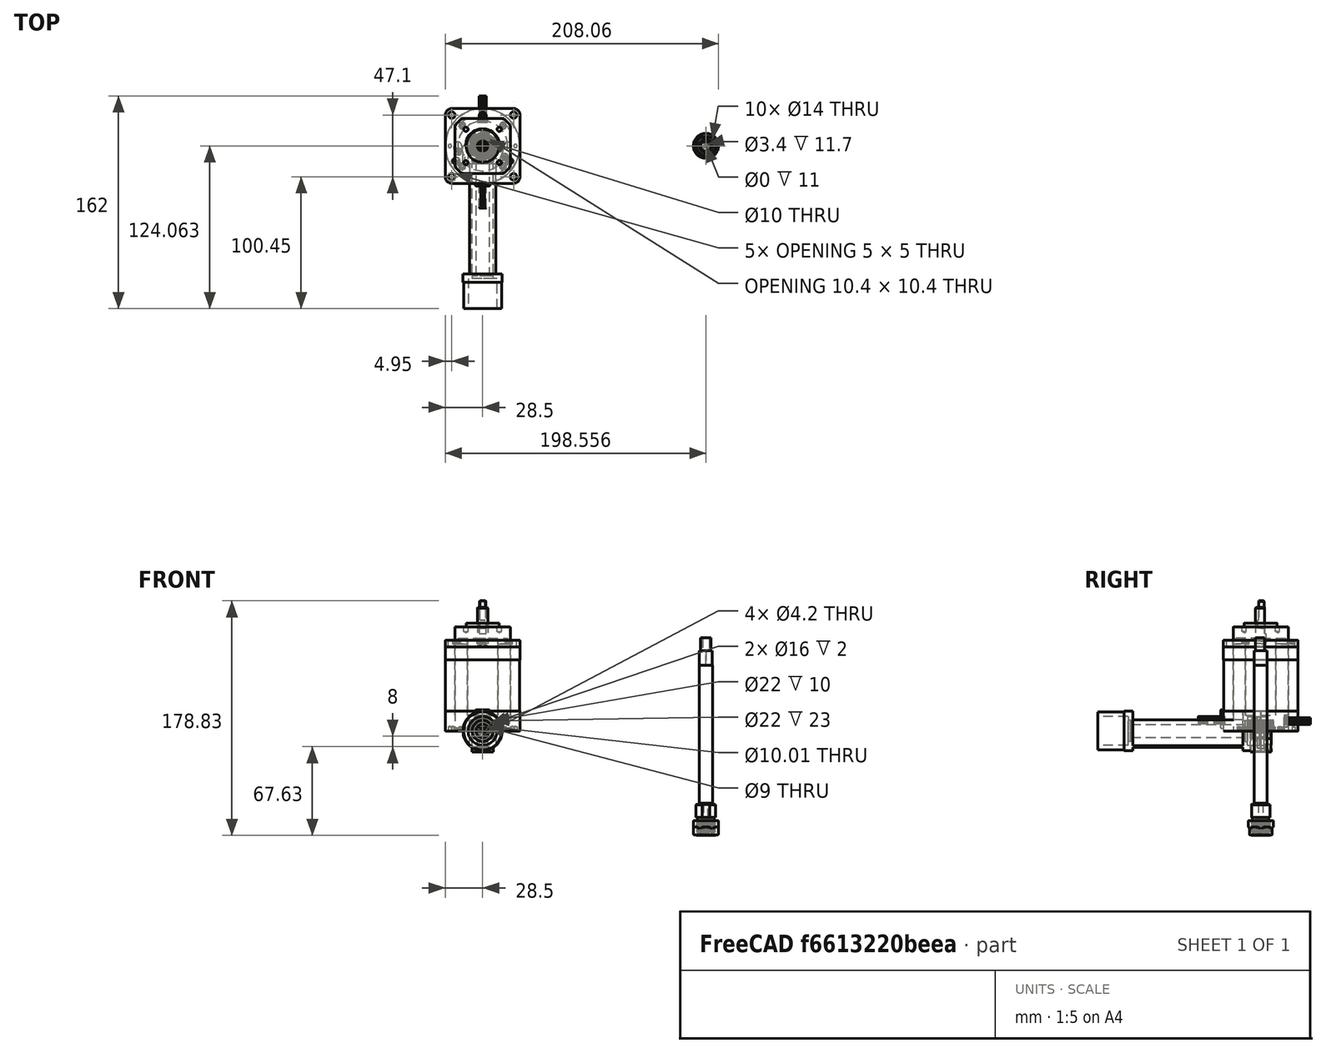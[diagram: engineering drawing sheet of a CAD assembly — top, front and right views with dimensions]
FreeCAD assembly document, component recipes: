
FREECAD ASSEMBLY — COMPONENT RECIPES ("ToolPostDrill")

This assembly document has 13 components, labeled P0..P12 below (a component is one placed body or linked part). 8 of them carry a construction recipe — the FreeCAD feature program that regenerates the part from scratch, quoted from this document or its linked companion documents; the rest are supplied as boundary geometry only. No exploded tour is included for this assembly.
COMPONENT P0 — geometry summary ("Bearing"; no construction recipe available for this part):
  bounding box: 22.0 x 22.0 x 6.0 mm
  tessellated surface: 480 triangles
  volume: 1254 mm^3 (43% of its bounding box)
  symmetry: 2-fold rotationally symmetric about the x axis; 4-fold rotationally symmetric about the y axis; 2-fold rotationally symmetric about the z axis; mirror-symmetric across its y mid-plane, z mid-plane
COMPONENT P1 — recipe-attached ("BLDC adapter", modeled in this document).
Construction recipe (the document's own serialized feature program — sketch geometry with constraints, then the solid features built on it; lengths are millimeters unless a unit is written):

FEATURE [Sketcher::SketchObject] Sketch017
  FullyConstrained = true
  MapMode = 5
  Support = -> [XY_Plane019]
  expr: Constraints[2] = Spreadsheet.ShaftDiameter
  expr: Constraints[3] = Spreadsheet.SpacerOuterDiameter
  sketch-geometry (2):
    g0: Circle CenterX=0 CenterY=0 CenterZ=0 NormalX=0 NormalY=0 NormalZ=1 AngleXU=0 Radius=5
    g1: Circle CenterX=0 CenterY=0 CenterZ=0 NormalX=0 NormalY=0 NormalZ=1 AngleXU=0 Radius=10.95
  constraints (4):
    c: Coincident(g0,g-1)
    c: Coincident(g1,g0)
    c: Diameter(g0) = 10
    c: Diameter(g1) = 21.9
FEATURE [PartDesign::Pad] Pad007
  Direction = (0,0,1)
  Length = 4
  Length2 = 10
  Profile = -> Sketch017
  ReferenceAxis = -> Sketch017 [N_Axis]
  Type = 0
  expr: Length = Spreadsheet.FrontSpacerWidth
FEATURE [PartDesign::Chamfer] Chamfer
  Angle = 45
  Base = -> Pad007 [Face4,Face3]
  BaseFeature = -> Pad007
  ChamferType = 0
  FlipDirection = false
  Size = 0.25
  Size2 = 1
  SupportTransform = false
  UseAllEdges = false
FEATURE [Sketcher::SketchObject] Sketch023
  FullyConstrained = true
  MapMode = 5
  Placement = pos=(0,0,4) rot=(0,0,1;0rad)
  Support = -> [Pad007]
  expr: Constraints[2] = Spreadsheet.BearingInnerPocketDiameter
  expr: Constraints[3] = Spreadsheet.SpacerOuterDiameter
  sketch-geometry (2):
    g0: Circle CenterX=0 CenterY=0 CenterZ=0 NormalX=0 NormalY=0 NormalZ=1 AngleXU=0 Radius=8
    g1: Circle CenterX=0 CenterY=0 CenterZ=0 NormalX=0 NormalY=0 NormalZ=1 AngleXU=0 Radius=10.95
  constraints (4):
    c: Coincident(g0,g-1)
    c: Coincident(g1,g0)
    c: Diameter(g0) = 16
    c: Diameter(g1) = 21.9
FEATURE [PartDesign::Pocket] Pocket009
  BaseFeature = -> Chamfer
  Direction = (0,0,-1)
  Length = 1
  Length2 = 5
  Profile = -> Sketch023
  ReferenceAxis = -> Sketch023 [N_Axis]
  Type = 0
FEATURE [PartDesign::Body] Body005  label="Body006"
  Group = -> [Sketch017,Pad007,Chamfer,Sketch023,Pocket009]
  Origin = -> Origin019
  Tip = -> Pocket009
COMPONENT P2 — geometry summary ("TopSlide"; no construction recipe available for this part):
  bounding box: 180.0 x 86.8 x 80.0 mm
  tessellated surface: 68 triangles
  volume: 648582 mm^3 (52% of its bounding box)
COMPONENT P3 — geometry summary ("ConnectorHousing"; no construction recipe available for this part):
  bounding box: 49.0 x 36.9 x 28.0 mm
  tessellated surface: 568 triangles
  volume: 17478 mm^3 (35% of its bounding box)
  symmetry: mirror-symmetric across its y mid-plane
COMPONENT P4 — recipe-attached ("LockNut", modeled in this document).
Construction recipe (the document's own serialized feature program — sketch geometry with constraints, then the solid features built on it; lengths are millimeters unless a unit is written):

FEATURE [Sketcher::SketchObject] Sketch024
  FullyConstrained = true
  MapMode = 5
  Placement = pos=(0,0,0) rot=(0.57735,0.57735,0.57735;2.0944rad)
  Support = -> [YZ_Plane025]
  expr: Constraints[13] = Spreadsheet.LockNutThreadDiameter / 2
  expr: Constraints[14] = Spreadsheet.LockNutDiameter / 2
  expr: Constraints[15] = Spreadsheet.BearingDiameterBase / 2
  expr: Constraints[17] = Spreadsheet.LockNutThickness
  sketch-geometry (6):
    g0: LineSegment StartX=0 StartY=10.9 StartZ=0 EndX=4.5 EndY=10.9 EndZ=0
    g1: LineSegment StartX=4.5 StartY=10.9 StartZ=0 EndX=4.5 EndY=7 EndZ=0
    g2: LineSegment StartX=4.5 StartY=7 StartZ=0 EndX=5 EndY=7 EndZ=0
    g3: LineSegment StartX=5 StartY=7 StartZ=0 EndX=5 EndY=4.5 EndZ=0
    g4: LineSegment StartX=5 StartY=4.5 StartZ=0 EndX=0 EndY=4.5 EndZ=0
    g5: LineSegment StartX=0 StartY=4.5 StartZ=0 EndX=0 EndY=10.9 EndZ=0
  constraints (18):
    c: PointOnObject(g0,g-2)
    c: Horizontal(g0)
    c: Coincident(g0,g1)
    c: Vertical(g1)
    c: Coincident(g1,g2)
    c: Horizontal(g2)
    c: Coincident(g2,g3)
    c: Vertical(g3)
    c: Coincident(g3,g4)
    c: PointOnObject(g4,g-2)
    c: Horizontal(g4)
    c: Coincident(g4,g5)
    c: Coincident(g5,g0)
    c: DistanceY(g-1,g4) = 4.5
    c: DistanceY(g-1,g0) = 10.9
    c: DistanceY(g-1,g2) = 7
    c: DistanceX(g2,g2) = 0.5
    c: DistanceX(g4,g4) = 5
FEATURE [PartDesign::Revolution] Revolution
  Angle = 360
  Axis = (1e-16,1,-1e-16)
  Base = (0,0,0)
  Placement = pos=(0,0,0) rot=(0.57735,0.57735,0.57735;2.0944rad)
  Profile = -> Sketch024
  ReferenceAxis = -> Y_Axis025
FEATURE [Sketcher::SketchObject] Sketch025
  FullyConstrained = true
  MapMode = 5
  Placement = pos=(0,-5e-16,0) rot=(0.57735,0.57735,-0.57735;2.0944rad)
  Support = -> [Revolution]
  expr: Constraints[2] = Spreadsheet.LockNutBoltSeparation
  expr: Constraints[3] = Spreadsheet.LockNutBoltDiameter
  sketch-geometry (2):
    g0: Circle CenterX=0 CenterY=8 CenterZ=0 NormalX=0 NormalY=0 NormalZ=1 AngleXU=0 Radius=1.5
    g1: Circle CenterX=0 CenterY=-8 CenterZ=0 NormalX=0 NormalY=0 NormalZ=1 AngleXU=0 Radius=1.5
  constraints (5):
    c: PointOnObject(g0,g-2)
    c: Symmetric(g0,g1,g-1)
    c: DistanceY(g1,g0) = 16
    c: Diameter(g0) = 3
    c: Equal(g0,g1)
FEATURE [PartDesign::Pocket] Pocket010
  BaseFeature = -> Revolution
  Direction = (2e-16,1,-4e-16)
  Length = 5
  Length2 = 5
  Placement = pos=(0,0,0) rot=(0.57735,0.57735,0.57735;2.0944rad)
  Profile = -> Sketch025
  ReferenceAxis = -> Sketch025 [N_Axis]
  Type = 1
FEATURE [PartDesign::Body] Body007  label="LockNutNut"
  Group = -> [Sketch024,Revolution,Sketch025,Pocket010]
  Origin = -> Origin025
  Tip = -> Pocket010
FEATURE [Sketcher::SketchObject] Sketch026
  FullyConstrained = true
  MapMode = 5
  Placement = pos=(0,0,0) rot=(1,0,0;1.5708rad)
  Support = -> [XZ_Plane026]
  expr: Constraints[2] = Spreadsheet.LockNutThreadDiameter
  expr: Constraints[3] = Spreadsheet.LockNutBoltThreadDiameter
  expr: Constraints[5] = Spreadsheet.LockNutDiameter
  expr: Constraints[7] = Spreadsheet.LockNutBoltSeparation
  sketch-geometry (4):
    g0: Circle CenterX=0 CenterY=0 CenterZ=0 NormalX=0 NormalY=0 NormalZ=1 AngleXU=0 Radius=4.5
    g1: Circle CenterX=0 CenterY=0 CenterZ=0 NormalX=0 NormalY=0 NormalZ=1 AngleXU=0 Radius=10.9
    g2: Circle CenterX=-8 CenterY=0 CenterZ=0 NormalX=0 NormalY=0 NormalZ=1 AngleXU=0 Radius=1.25
    g3: Circle CenterX=8 CenterY=0 CenterZ=0 NormalX=0 NormalY=0 NormalZ=1 AngleXU=0 Radius=1.25
  constraints (9):
    c: Coincident(g0,g-1)
    c: Coincident(g1,g0)
    c: Diameter(g0) = 9
    c: Diameter(g2) = 2.5
    c: Equal(g2,g3)
    c: Diameter(g1) = 21.8
    c: Symmetric(g3,g2,g0)
    c: Distance(g2,g3) = 16
    c: PointOnObject(g2,g-1)
FEATURE [PartDesign::Pad] Pad009
  Direction = (0,-1,-2e-16)
  Length = 3
  Length2 = 10
  Placement = pos=(0,0,0) rot=(1,0,0;1.5708rad)
  Profile = -> Sketch026
  ReferenceAxis = -> Sketch026 [N_Axis]
  Type = 0
  expr: Length = Spreadsheet.LockNutWasherThickness
FEATURE [PartDesign::CoordinateSystem] Back
  AttacherType = Attacher::AttachEngine3D
  MapMode = 11
  Placement = pos=(0,-3,7e-16) rot=(0.57735,-0.57735,0.57735;2.0944rad)
  Support = -> [Pad009]
FEATURE [PartDesign::Body] Body008  label="LockNutDisk"
  Group = -> [Sketch026,Pad009,Back]
  Origin = -> Origin026
  Placement = pos=(0,-1,0) rot=(0,0,1;0rad)
  Tip = -> Pad009
COMPONENT P5 — recipe-attached ("Housing", modeled in this document).
Construction recipe (the document's own serialized feature program — sketch geometry with constraints, then the solid features built on it; lengths are millimeters unless a unit is written):

FEATURE [Sketcher::SketchObject] Sketch
  FullyConstrained = true
  MapMode = 5
  Placement = pos=(0,0,0) rot=(1,0,0;1.5708rad)
  Support = -> [XZ_Plane005]
  expr: Constraints[1] = Spreadsheet.HousingDiameter
  sketch-geometry (1):
    g0: Circle CenterX=0 CenterY=0 CenterZ=0 NormalX=0 NormalY=0 NormalZ=1 AngleXU=0 Radius=14.95
  constraints (2):
    c: Coincident(g0,g-1)
    c: Diameter(g0) = 29.9
FEATURE [PartDesign::Pad] Pad001  label="Housing001"
  Direction = (0,-1,-2e-16)
  Length = 124
  Length2 = 10
  Placement = pos=(0,0,0) rot=(1,0,0;1.5708rad)
  Profile = -> Sketch
  ReferenceAxis = -> Sketch [N_Axis]
  Type = 0
  expr: Length = Spreadsheet.HousingLength
FEATURE [Sketcher::SketchObject] Sketch001
  FullyConstrained = true
  MapMode = 5
  Placement = pos=(0,0,0) rot=(-1,0,0;1.5708rad)
  Support = -> [Pad001]
  expr: Constraints[1] = Spreadsheet.BearingDiameter
  sketch-geometry (1):
    g0: Circle CenterX=0 CenterY=0 CenterZ=0 NormalX=0 NormalY=0 NormalZ=1 AngleXU=0 Radius=11
  constraints (2):
    c: Coincident(g0,g-1)
    c: Diameter(g0) = 22
FEATURE [PartDesign::Pocket] Pocket  label="FrontBearingPocket"
  BaseFeature = -> Pad001
  Direction = (0,-1,-2e-16)
  Length = 10
  Length2 = 5
  Placement = pos=(0,0,0) rot=(1,0,0;1.5708rad)
  Profile = -> Sketch001
  ReferenceAxis = -> Sketch001 [N_Axis]
  Type = 0
  expr: Length = Spreadsheet.FrontBearingPocketDepth
FEATURE [Sketcher::SketchObject] Sketch002
  FullyConstrained = true
  MapMode = 5
  Placement = pos=(0,-10,0) rot=(-1,0,0;1.5708rad)
  Support = -> [Pocket]
  expr: Constraints[1] = Spreadsheet.ShaftBoringDiameter
  sketch-geometry (1):
    g0: Circle CenterX=0 CenterY=0 CenterZ=0 NormalX=0 NormalY=0 NormalZ=1 AngleXU=0 Radius=5.005
  constraints (2):
    c: Coincident(g0,g-1)
    c: Diameter(g0) = 10.01
FEATURE [Sketcher::SketchObject] Sketch004
  AttachmentOffset = pos=(0,0,13.5) rot=(0,0,1;0rad)
  FullyConstrained = true
  MapMode = 5
  Placement = pos=(0,-13.5,-3e-15) rot=(1,0,0;1.5708rad)
  Support = -> [XZ_Plane005]
  expr: .AttachmentOffset.Base.z = Spreadsheet.ToolPostPocketPositionH
  expr: Constraints[13] = Spreadsheet.HousingDiameter + 1
  expr: Constraints[2] = Spreadsheet.ToolHeight
  expr: Constraints[3] = Spreadsheet.HousingDiameter + 1
  expr: Constraints[5] = Spreadsheet.ToolHolderHeigth
  expr: Constraints[7] = Spreadsheet.ShaftPosition
  sketch-geometry (13):
    g0: LineSegment StartX=-9.29289 StartY=-12.5 StartZ=0 EndX=9.29289 EndY=-12.5 EndZ=0
    g1: LineSegment StartX=15.45 StartY=-15.45 StartZ=0 EndX=-15.45 EndY=-15.45 EndZ=0
    g2: LineSegment StartX=-10 StartY=8.5 StartZ=0 EndX=10 EndY=8.5 EndZ=0
    g3: LineSegment StartX=-10 StartY=-11.7929 StartZ=0 EndX=-10 EndY=8.5 EndZ=0
    g4: LineSegment StartX=10 StartY=8.5 StartZ=0 EndX=10 EndY=-11.7929 EndZ=0
    g5: LineSegment StartX=-15.45 StartY=-15.45 StartZ=0 EndX=-15.45 EndY=15.45 EndZ=0
    g6: LineSegment StartX=-15.45 StartY=15.45 StartZ=0 EndX=15.45 EndY=15.45 EndZ=0
    g7: LineSegment StartX=15.45 StartY=15.45 StartZ=0 EndX=15.45 EndY=-15.45 EndZ=0
    g8: GeomPoint X=-15.45 Y=15.45 Z=0
    g9: GeomPoint X=-10 Y=8.5 Z=0
    g10: GeomPoint X=10 Y=8.5 Z=0
    g11: LineSegment StartX=-10 StartY=-11.7929 StartZ=0 EndX=-9.29289 EndY=-12.5 EndZ=0
    g12: LineSegment StartX=10 StartY=-11.7929 StartZ=0 EndX=9.29289 EndY=-12.5 EndZ=0
  constraints (33):
    c: Horizontal(g0)
    c: Symmetric(g1,g1,g-2)
    c: DistanceY(g0,g-1) = 12.5
    c: DistanceX(g1,g1) = 30.9
    c: Symmetric(g9,g10,g-2)
    c: DistanceY(g0,g10) = 21
    c: Vertical(g3)
    c: DistanceX(g-1,g10) = 10
    c: Coincident(g1,g5)
    c: Vertical(g5)
    c: Horizontal(g6)
    c: Coincident(g6,g7)
    c: Coincident(g7,g1)
    c: DistanceY(g7,g7) = 30.9
    c: PointOnObject(g8,g6)
    c: PointOnObject(g8,g5)
    c: Symmetric(g6,g1,g-1)
    c: PointOnObject(g9,g2)
    c: PointOnObject(g9,g3)
    c: PointOnObject(g10,g2)
    c: PointOnObject(g10,g4)
    c: Vertical(g4)
    c: Coincident(g3,g2)
    c: Coincident(g4,g2)
    c: Coincident(g5,g6)
    c: Coincident(g4,g12)
    c: Coincident(g12,g0)
    c: Angle(g12,g0) = 2.35619
    c: Coincident(g3,g11)
    c: Coincident(g11,g0)
    c: Angle(g0,g11) = 2.35619
    c: Distance(g11) = 1
    c: Equal(g11,g12)
FEATURE [Sketcher::SketchObject] Sketch021
  FullyConstrained = true
  MapMode = 5
  Placement = pos=(0,-10,0) rot=(-1,0,0;1.5708rad)
  Support = -> [Pocket]
  expr: Constraints[1] = Spreadsheet.BearingInnerPocketDiameter
  sketch-geometry (1):
    g0: Circle CenterX=0 CenterY=0 CenterZ=0 NormalX=0 NormalY=0 NormalZ=1 AngleXU=0 Radius=8
  constraints (2):
    c: Coincident(g0,g-1)
    c: Diameter(g0) = 16
FEATURE [PartDesign::Pocket] Pocket007  label="FrontBearingInnerPocket"
  BaseFeature = -> Pocket
  Direction = (0,-1,-2e-16)
  Length = 2
  Length2 = 5
  Placement = pos=(0,0,0) rot=(1,0,0;1.5708rad)
  Profile = -> Sketch021
  ReferenceAxis = -> Sketch021 [N_Axis]
  Type = 0
  expr: Length = Spreadsheet.BearingInnerPocketDepth
FEATURE [PartDesign::Pocket] Pocket001  label="ShaftPocket"
  BaseFeature = -> Pocket007
  Direction = (0,-1,-2e-16)
  Length = 5
  Length2 = 5
  Placement = pos=(0,0,0) rot=(1,0,0;1.5708rad)
  Profile = -> Sketch002
  ReferenceAxis = -> Sketch002 [N_Axis]
  Type = 1
FEATURE [Sketcher::SketchObject] Sketch003
  FullyConstrained = true
  MapMode = 5
  Placement = pos=(0,-124,3e-16) rot=(1,0,0;1.5708rad)
  Support = -> [Pocket001]
  expr: Constraints[1] = Spreadsheet.BearingDiameter
  sketch-geometry (1):
    g0: Circle CenterX=0 CenterY=0 CenterZ=0 NormalX=0 NormalY=0 NormalZ=1 AngleXU=0 Radius=11
  constraints (2):
    c: Coincident(g0,g-1)
    c: Diameter(g0) = 22
FEATURE [PartDesign::Pocket] Pocket002  label="BackBearingPocket"
  BaseFeature = -> Pocket001
  Direction = (0,1,2e-16)
  Length = 23
  Length2 = 5
  Placement = pos=(0,0,0) rot=(1,0,0;1.5708rad)
  Profile = -> Sketch003
  ReferenceAxis = -> Sketch003 [N_Axis]
  Type = 0
  expr: Length = Spreadsheet.BackBearingPocketDepth
FEATURE [Sketcher::SketchObject] Sketch022
  FullyConstrained = true
  MapMode = 5
  Placement = pos=(0,-101,2.24e-14) rot=(1,0,0;1.5708rad)
  Support = -> [Pocket002]
  expr: Constraints[1] = Spreadsheet.BearingInnerPocketDiameter
  sketch-geometry (1):
    g0: Circle CenterX=0 CenterY=0 CenterZ=0 NormalX=0 NormalY=0 NormalZ=1 AngleXU=0 Radius=8
  constraints (2):
    c: Coincident(g0,g-1)
    c: Diameter(g0) = 16
FEATURE [PartDesign::Pocket] Pocket008  label="BackBearingInnerPocket"
  BaseFeature = -> Pocket002
  Direction = (0,1,-2e-16)
  Length = 2
  Length2 = 5
  Placement = pos=(0,0,0) rot=(1,0,0;1.5708rad)
  Profile = -> Sketch022
  ReferenceAxis = -> Sketch022 [N_Axis]
  Type = 0
  expr: Length = Spreadsheet.BearingInnerPocketDepth
FEATURE [PartDesign::Pocket] Pocket003  label="ToolPostPocket"
  BaseFeature = -> Pocket008
  Direction = (0,1,2e-16)
  Length = 84
  Length2 = 5
  Placement = pos=(0,0,0) rot=(1,0,0;1.5708rad)
  Profile = -> Sketch004
  ReferenceAxis = -> Sketch004 [N_Axis]
  Reversed = true
  Type = 0
  expr: Length = Spreadsheet.ToolPostPocketLength
FEATURE [Sketcher::SketchObject] Sketch015
  FullyConstrained = true
  MapMode = 5
  Placement = pos=(0,-124,3e-16) rot=(1,0,0;1.5708rad)
  Support = -> [Pocket003]
  expr: Constraints[1] = Spreadsheet.MountingShaftDiameter
  expr: Constraints[3] = Spreadsheet.HousingDiameter + 1
  sketch-geometry (2):
    g0: Circle CenterX=0 CenterY=0 CenterZ=0 NormalX=0 NormalY=0 NormalZ=1 AngleXU=0 Radius=14.45
    g1: Circle CenterX=0 CenterY=0 CenterZ=0 NormalX=0 NormalY=0 NormalZ=1 AngleXU=0 Radius=15.45
  constraints (4):
    c: Coincident(g0,g-1)
    c: Diameter(g0) = 28.9
    c: Coincident(g1,g0)
    c: Diameter(g1) = 30.9
FEATURE [PartDesign::Pocket] Pocket005  label="MountingShaftPocket"
  BaseFeature = -> Pocket003
  Direction = (0,1,2e-16)
  Length = 20
  Length2 = 5
  Placement = pos=(0,0,0) rot=(1,0,0;1.5708rad)
  Profile = -> Sketch015
  ReferenceAxis = -> Sketch015 [N_Axis]
  Type = 0
  expr: Length = Spreadsheet.MountingShaftLength
FEATURE [PartDesign::Body] Body001  label="HousingBody"
  Group = -> [Sketch,Pad001,Sketch001,Pocket,Pocket007,Sketch002,Pocket001,Sketch003,Pocket002,Pocket008,Sketch004,Pocket003,Sketch015,Pocket005,Sketch021,Sketch022]
  Origin = -> Origin005
  Tip = -> Pocket005
COMPONENT P6 — geometry summary ("Spindle"; no construction recipe available for this part):
  bounding box: 150.6 x 19.0 x 18.8 mm
  tessellated surface: 3,004 triangles
  volume: 13659 mm^3 (25% of its bounding box)
COMPONENT P7 — geometry summary ("BLDCmotor"; no construction recipe available for this part):
  bounding box: 94.1 x 76.0 x 57.0 mm
  tessellated surface: 5,510 triangles
  volume: 180203 mm^3 (44% of its bounding box)
COMPONENT P8 — recipe-attached ("BevelGearSpindle", modeled in this document).
Construction recipe (the document's own serialized feature program — sketch geometry with constraints, then the solid features built on it; lengths are millimeters unless a unit is written):

FEATURE [Sketcher::SketchObject] Sketch031
  FullyConstrained = true
  MapMode = 5
  Support = -> [XY_Plane032]
  expr: Constraints[1] = Spreadsheet.GearShaftOuterDiameter
  sketch-geometry (1):
    g0: Circle CenterX=0 CenterY=0 CenterZ=0 NormalX=0 NormalY=0 NormalZ=1 AngleXU=0 Radius=8
  constraints (2):
    c: Coincident(g0,g-1)
    c: Diameter(g0) = 16
FEATURE [PartDesign::Pad] Pad012
  Direction = (0,0,1)
  Length = 6
  Length2 = 10
  Profile = -> Sketch031
  ReferenceAxis = -> Sketch031 [N_Axis]
  Reversed = true
  Type = 0
  expr: Length = Spreadsheet.GearLengthSpindle - Spreadsheet.GearHeight
FEATURE [Sketcher::SketchObject] Sketch032
  AttachmentOffset = pos=(0,0,-6) rot=(0,0,1;0rad)
  FullyConstrained = true
  MapMode = 5
  Placement = pos=(0,0,-6) rot=(0,0,1;0rad)
  Support = -> [XY_Plane032]
  expr: .AttachmentOffset.Base.z = -Spreadsheet.GearShaftLength
  expr: Constraints[4] = Spreadsheet.ShaftCouplerInnerDiameter
  expr: Constraints[5] = Spreadsheet.ShaftCouplerInnerDiameter / 2 - 1
  sketch-geometry (2):
    g0: ArcOfCircle CenterX=0 CenterY=0 CenterZ=0 NormalX=0 NormalY=0 NormalZ=1 AngleXU=0 Radius=4.075 StartAngle=2.28655 EndAngle=7.13823
    g1: LineSegment StartX=-2.67395 StartY=3.075 StartZ=0 EndX=2.67395 EndY=3.075 EndZ=0
  constraints (6):
    c: Coincident(g0,g-1)
    c: Horizontal(g1)
    c: Coincident(g0,g1)
    c: Coincident(g0,g1)
    c: Diameter(g0) = 8.15
    c: DistanceY(g0,g0) = 3.075
FEATURE [PartDesign::Pocket] Pocket011  label="ShaftPocket001"
  BaseFeature = -> Pad012
  Direction = (0,0,-1)
  Length = 11
  Length2 = 5
  Profile = -> Sketch032
  ReferenceAxis = -> Sketch032 [N_Axis]
  Reversed = true
  Type = 1
  expr: Length = Spreadsheet.GearShaftPocketDepth
FEATURE [PartDesign::Chamfer] Chamfer002  label="Chamferhaft"
  Angle = 45
  Base = -> Pocket011 [Edge6,Edge7]
  BaseFeature = -> Pocket011
  ChamferType = 0
  FlipDirection = false
  Size = 0.3
  Size2 = 1
  SupportTransform = false
  UseAllEdges = false
FEATURE [PartDesign::FeaturePython] BevelGear002  # WARN: FeaturePython — macro-defined, semantics opaque (R4)
  AttacherType = Attacher::AttachEngine3D
  BaseFeature = -> Chamfer002
  angular_backlash = 0
  backlash = 0
  beta = 0
  clearance = 0.1
  dw = 18
  height = 8
  module = 1
  numpoints = 6
  pitch_angle = 45
  pressure_angle = 20
  reset_origin = true
  teeth = 18
  version = 0.0.4
  expr: angular_backlash = backlash / dw * 360° / pi
  expr: beta = Spreadsheet.GearHelix
  expr: dw = teeth * module
  expr: height = Spreadsheet.GearHeight
  expr: module = Spreadsheet.GearModule
  expr: teeth = Spreadsheet.GearTeeth
FEATURE [Sketcher::SketchObject] Sketch035
  FullyConstrained = true
  MapMode = 5
  Support = -> [XY_Plane032]
  expr: Constraints[1] = Spreadsheet.GearTeethPocketDiameter
  expr: Constraints[3] = Spreadsheet.GearTeethPocketDiameter * 2
  sketch-geometry (2):
    g0: Circle CenterX=0 CenterY=0 CenterZ=0 NormalX=0 NormalY=0 NormalZ=1 AngleXU=0 Radius=9
    g1: Circle CenterX=0 CenterY=0 CenterZ=0 NormalX=0 NormalY=0 NormalZ=1 AngleXU=0 Radius=18
  constraints (4):
    c: Coincident(g0,g-1)
    c: Diameter(g0) = 18
    c: Coincident(g1,g0)
    c: Diameter(g1) = 36
FEATURE [PartDesign::Pocket] Pocket015  label="TeethPocket001"
  BaseFeature = -> BevelGear002
  Direction = (0,0,-1)
  Length = 5
  Length2 = 5
  Profile = -> Sketch035
  ReferenceAxis = -> Sketch035 [N_Axis]
  Reversed = true
  Type = 1
FEATURE [PartDesign::Pocket] Pocket019  label="GearPocket"
  BaseFeature = -> Pocket015
  Direction = (0,0,-1)
  Length = 5
  Length2 = 5
  Profile = -> Pocket015 [Face35]
  Type = 1
FEATURE [Sketcher::SketchObject] Sketch038  label="LockBoltPocket"
  AttachmentOffset = pos=(0,0,-8) rot=(0,0,1;0rad)
  FullyConstrained = true
  MapMode = 5
  Placement = pos=(0,8,1.8e-15) rot=(1,0,0;1.5708rad)
  Support = -> [XZ_Plane032]
  expr: .AttachmentOffset.Base.z = -Spreadsheet.GearShaftOuterDiameter / 2
  expr: Constraints[1] = Spreadsheet.GearLockBoltThreadDiameter
  expr: Constraints[2] = Spreadsheet.GearShaftLength / 2
  sketch-geometry (1):
    g0: Circle CenterX=0 CenterY=-3 CenterZ=0 NormalX=0 NormalY=0 NormalZ=1 AngleXU=0 Radius=2.1
  constraints (3):
    c: PointOnObject(g0,g-2)
    c: Diameter(g0) = 4.2
    c: DistanceY(g0,g-1) = 3
FEATURE [PartDesign::Pocket] Pocket020  label="LockBoltPocket020"
  BaseFeature = -> Pocket019
  Direction = (0,1,2e-16)
  Length = 8
  Length2 = 5
  Profile = -> Sketch038
  ReferenceAxis = -> Sketch038 [N_Axis]
  Reversed = true
  Type = 0
  expr: Length = Spreadsheet.GearShaftOuterDiameter / 2
FEATURE [PartDesign::Body] Body011
  Group = -> [Sketch031,Pad012,Sketch032,Pocket011,Chamfer002,BevelGear002,Sketch035,Pocket015,Pocket019,Sketch038,Pocket020]
  Origin = -> Origin032
  Placement = pos=(0,0,0) rot=(0,0,1;0.139626rad)
  Tip = -> Pocket020
COMPONENT P9 — recipe-attached ("BevelGearBLDC", modeled in this document).
Construction recipe (the document's own serialized feature program — sketch geometry with constraints, then the solid features built on it; lengths are millimeters unless a unit is written):

FEATURE [Sketcher::SketchObject] Sketch033
  FullyConstrained = true
  MapMode = 5
  Support = -> [XY_Plane034]
  expr: Constraints[1] = Spreadsheet.GearShaftOuterDiameter
  sketch-geometry (1):
    g0: Circle CenterX=0 CenterY=0 CenterZ=0 NormalX=0 NormalY=0 NormalZ=1 AngleXU=0 Radius=8
  constraints (2):
    c: Coincident(g0,g-1)
    c: Diameter(g0) = 16
FEATURE [PartDesign::Pad] Pad013
  Direction = (0,0,1)
  Length = 16
  Length2 = 10
  Profile = -> Sketch033
  ReferenceAxis = -> Sketch033 [N_Axis]
  Reversed = true
  Type = 0
  expr: Length = Spreadsheet.GearLengthBLDC - Spreadsheet.GearHeight
FEATURE [Sketcher::SketchObject] Sketch036
  FullyConstrained = true
  MapMode = 5
  Support = -> [XY_Plane034]
  expr: Constraints[2] = Spreadsheet.GearTeethPocketDiameter * 2
  expr: Constraints[3] = Spreadsheet.GearTeethPocketDiameter
  sketch-geometry (2):
    g0: Circle CenterX=0 CenterY=0 CenterZ=0 NormalX=0 NormalY=0 NormalZ=1 AngleXU=0 Radius=18
    g1: Circle CenterX=0 CenterY=0 CenterZ=0 NormalX=0 NormalY=0 NormalZ=1 AngleXU=0 Radius=9
  constraints (4):
    c: Coincident(g0,g-1)
    c: Coincident(g1,g0)
    c: Diameter(g0) = 36
    c: Diameter(g1) = 18
FEATURE [Sketcher::SketchObject] Sketch034
  FullyConstrained = true
  MapMode = 5
  Support = -> [XY_Plane034]
  expr: Constraints[4] = Spreadsheet.ShaftCouplerInnerDiameter
  expr: Constraints[5] = Spreadsheet.ShaftCouplerInnerDiameter / 2 - 1
  sketch-geometry (2):
    g0: ArcOfCircle CenterX=0 CenterY=0 CenterZ=0 NormalX=0 NormalY=0 NormalZ=1 AngleXU=0 Radius=4.075 StartAngle=2.28655 EndAngle=7.13823
    g1: LineSegment StartX=-2.67395 StartY=3.075 StartZ=0 EndX=2.67395 EndY=3.075 EndZ=0
  constraints (6):
    c: Coincident(g0,g-1)
    c: Horizontal(g1)
    c: Coincident(g0,g1)
    c: Coincident(g0,g1)
    c: Diameter(g0) = 8.15
    c: DistanceY(g0,g0) = 3.075
FEATURE [PartDesign::Pocket] Pocket013  label="ShaftPocket002"
  BaseFeature = -> Pad013
  Direction = (0,0,-1)
  Length = 11
  Length2 = 5
  Profile = -> Sketch034
  ReferenceAxis = -> Sketch034 [N_Axis]
  Type = 1
  expr: Length = Spreadsheet.GearShaftPocketDepth
FEATURE [PartDesign::Chamfer] Chamfer003  label="ShaftChamfer"
  Angle = 45
  Base = -> Pocket013 [Edge6,Edge7]
  BaseFeature = -> Pocket013
  ChamferType = 0
  FlipDirection = false
  Size = 0.3
  Size2 = 1
  SupportTransform = false
  UseAllEdges = false
FEATURE [PartDesign::FeaturePython] BevelGear003  # WARN: FeaturePython — macro-defined, semantics opaque (R4)
  AttacherType = Attacher::AttachEngine3D
  BaseFeature = -> Chamfer003
  angular_backlash = 0
  backlash = 0
  beta = 0
  clearance = 0.1
  dw = 18
  height = 8
  module = 1
  numpoints = 6
  pitch_angle = 45
  pressure_angle = 20
  reset_origin = true
  teeth = 18
  version = 0.0.4
  expr: angular_backlash = backlash / dw * 360° / pi
  expr: beta = Spreadsheet.GearHelix
  expr: dw = teeth * module
  expr: height = Spreadsheet.GearHeight
  expr: module = Spreadsheet.GearModule
  expr: teeth = Spreadsheet.GearTeeth
FEATURE [PartDesign::Pocket] Pocket016  label="TeethPocket"
  BaseFeature = -> BevelGear003
  Direction = (0,0,-1)
  Length = 5
  Length2 = 5
  Profile = -> Sketch036
  ReferenceAxis = -> Sketch036 [N_Axis]
  Reversed = true
  Type = 1
FEATURE [PartDesign::Pocket] Pocket017  label="GearShaftPocket"
  BaseFeature = -> Pocket016
  Direction = (0,0,-1)
  Length = 5
  Length2 = 5
  Profile = -> Pocket016 [Face35]
  Type = 1
FEATURE [Sketcher::SketchObject] Sketch037
  AttachmentOffset = pos=(0,0,-9) rot=(0,0,1;0rad)
  FullyConstrained = true
  MapMode = 5
  Placement = pos=(0,9,2e-15) rot=(1,0,0;1.5708rad)
  Support = -> [XZ_Plane034]
  expr: .AttachmentOffset.Base.z = -Spreadsheet.GearTeethPocketDiameter / 2
  expr: Constraints[2] = Spreadsheet.GearLockBoltThreadDiameter
  expr: Constraints[4] = Spreadsheet.GearLockBoltSeparation
  expr: Constraints[5] = Spreadsheet.GearLockBoltPosition
  sketch-geometry (2):
    g0: Circle CenterX=0 CenterY=-4 CenterZ=0 NormalX=0 NormalY=0 NormalZ=1 AngleXU=0 Radius=2.1
    g1: Circle CenterX=0 CenterY=-12 CenterZ=0 NormalX=0 NormalY=0 NormalZ=1 AngleXU=0 Radius=2.1
  constraints (6):
    c: PointOnObject(g0,g-2)
    c: PointOnObject(g1,g-2)
    c: Diameter(g0) = 4.2
    c: Equal(g0,g1)
    c: DistanceY(g1,g0) = 8
    c: DistanceY(g0,g-1) = 4
FEATURE [PartDesign::Pocket] Pocket018  label="LockBoltPocket021"
  BaseFeature = -> Pocket017
  Direction = (0,1,2e-16)
  Length = 9
  Length2 = 5
  Profile = -> Sketch037
  ReferenceAxis = -> Sketch037 [N_Axis]
  Reversed = true
  Type = 0
  expr: Length = Spreadsheet.GearTeethPocketDiameter / 2
FEATURE [PartDesign::Body] Body012
  Group = -> [Sketch033,Pad013,Sketch034,Pocket013,Chamfer003,BevelGear003,Sketch036,Pocket016,Pocket017,Sketch037,Pocket018]
  Origin = -> Origin034
  Tip = -> Pocket018
COMPONENT P10 — recipe-attached ("SpurGearSpindle", modeled in this document).
Construction recipe (the document's own serialized feature program — sketch geometry with constraints, then the solid features built on it; lengths are millimeters unless a unit is written):

FEATURE [Sketcher::SketchObject] Sketch039
  FullyConstrained = true
  MapMode = 5
  Support = -> [XY_Plane036]
  expr: Constraints[1] = Spreadsheet.GearShaftOuterDiameter
  sketch-geometry (1):
    g0: Circle CenterX=0 CenterY=0 CenterZ=0 NormalX=0 NormalY=0 NormalZ=1 AngleXU=0 Radius=8
  constraints (2):
    c: Coincident(g0,g-1)
    c: Diameter(g0) = 16
FEATURE [PartDesign::Pad] Pad014
  Direction = (0,0,1)
  Length = 6
  Length2 = 10
  Profile = -> Sketch039
  ReferenceAxis = -> Sketch039 [N_Axis]
  Reversed = true
  Type = 0
  expr: Length = Spreadsheet.GearLengthSpindle - Spreadsheet.GearHeight
FEATURE [Sketcher::SketchObject] Sketch040
  AttachmentOffset = pos=(0,0,-6) rot=(0,0,1;0rad)
  FullyConstrained = true
  MapMode = 5
  Placement = pos=(0,0,-6) rot=(0,0,1;0rad)
  Support = -> [XY_Plane036]
  expr: .AttachmentOffset.Base.z = -Spreadsheet.GearShaftLength
  expr: Constraints[4] = Spreadsheet.ShaftCouplerInnerDiameter
  expr: Constraints[5] = Spreadsheet.ShaftCouplerInnerDiameter / 2 - 1
  sketch-geometry (2):
    g0: ArcOfCircle CenterX=0 CenterY=0 CenterZ=0 NormalX=0 NormalY=0 NormalZ=1 AngleXU=0 Radius=4.075 StartAngle=2.28655 EndAngle=7.13823
    g1: LineSegment StartX=-2.67395 StartY=3.075 StartZ=0 EndX=2.67395 EndY=3.075 EndZ=0
  constraints (6):
    c: Coincident(g0,g-1)
    c: Horizontal(g1)
    c: Coincident(g0,g1)
    c: Coincident(g0,g1)
    c: Diameter(g0) = 8.15
    c: DistanceY(g0,g0) = 3.075
FEATURE [PartDesign::Pocket] Pocket021  label="ShaftPocket003"
  BaseFeature = -> Pad014
  Direction = (0,0,-1)
  Length = 11
  Length2 = 5
  Profile = -> Sketch040
  ReferenceAxis = -> Sketch040 [N_Axis]
  Reversed = true
  Type = 1
  expr: Length = Spreadsheet.GearShaftPocketDepth
FEATURE [PartDesign::Chamfer] Chamfer004  label="Chamferhaft001"
  Angle = 45
  Base = -> Pocket021 [Edge6,Edge7]
  BaseFeature = -> Pocket021
  ChamferType = 0
  FlipDirection = false
  Size = 0.3
  Size2 = 1
  SupportTransform = false
  UseAllEdges = false
FEATURE [Sketcher::SketchObject] Sketch042  label="LockBoltPocket023"
  AttachmentOffset = pos=(0,0,-8) rot=(0,0,1;0rad)
  FullyConstrained = true
  MapMode = 5
  Placement = pos=(0,8,1.8e-15) rot=(1,0,0;1.5708rad)
  Support = -> [XZ_Plane036]
  expr: .AttachmentOffset.Base.z = -Spreadsheet.GearShaftOuterDiameter / 2
  expr: Constraints[1] = Spreadsheet.GearLockBoltThreadDiameter
  expr: Constraints[2] = Spreadsheet.GearShaftLength / 2
  sketch-geometry (1):
    g0: Circle CenterX=0 CenterY=-3 CenterZ=0 NormalX=0 NormalY=0 NormalZ=1 AngleXU=0 Radius=2.1
  constraints (3):
    c: PointOnObject(g0,g-2)
    c: Diameter(g0) = 4.2
    c: DistanceY(g0,g-1) = 3
FEATURE [PartDesign::Pocket] Pocket024  label="LockBoltPocket022"
  BaseFeature = -> Chamfer004
  Direction = (0,1,2e-16)
  Length = 8
  Length2 = 5
  Profile = -> Sketch042
  ReferenceAxis = -> Sketch042 [N_Axis]
  Reversed = true
  Type = 0
  expr: Length = Spreadsheet.GearShaftOuterDiameter / 2
FEATURE [PartDesign::FeaturePython] InvoluteGear  # WARN: FeaturePython — macro-defined, semantics opaque (R4)
  AttacherType = Attacher::AttachEngine3D
  BaseFeature = -> Pocket024
  angular_backlash = 0
  backlash = 0
  beta = 0
  clearance = 0.25
  da = 20
  df = 15.5
  double_helix = false
  dw = 18
  head = 0
  head_fillet = 0
  height = 8
  module = 1
  numpoints = 6
  pressure_angle = 20
  properties_from_tool = false
  reversed_backlash = false
  root_fillet = 0
  shift = 0
  simple = false
  teeth = 18
  transverse_pitch = 3.14159
  undercut = false
  version = 0.0.4
  expr: angular_backlash = backlash / dw * 360° / pi
  expr: dw = teeth * module
  expr: height = Spreadsheet.GearHeight
  expr: module = Spreadsheet.GearModule
  expr: teeth = Spreadsheet.GearTeeth
FEATURE [PartDesign::ShapeBinder] ShapeBinder
  Placement = pos=(0,0,-6) rot=(0,0,1;0rad)
  Support = -> [Sketch040]
  TraceSupport = false
FEATURE [PartDesign::Pocket] Pocket025  label="ShaftPocket004"
  BaseFeature = -> InvoluteGear
  Direction = (0,0,-1)
  Length = 5
  Length2 = 5
  Profile = -> ShapeBinder
  Reversed = true
  Type = 1
FEATURE [PartDesign::Body] Body013  label="SpurGear"
  Group = -> [Sketch039,Pad014,Sketch040,Pocket021,Chamfer004,Sketch042,Pocket024,InvoluteGear,ShapeBinder,Pocket025]
  Origin = -> Origin036
  Placement = pos=(0,0,0) rot=(0,0,1;0.139626rad)
  Tip = -> Pocket025
COMPONENT P11 — recipe-attached ("SpurGearBLDC", modeled in this document).
Construction recipe (the document's own serialized feature program — sketch geometry with constraints, then the solid features built on it; lengths are millimeters unless a unit is written):

FEATURE [Sketcher::SketchObject] Sketch045
  FullyConstrained = true
  MapMode = 5
  Support = -> [XY_Plane039]
  expr: Constraints[1] = Spreadsheet.GearShaftOuterDiameter
  sketch-geometry (1):
    g0: Circle CenterX=0 CenterY=0 CenterZ=0 NormalX=0 NormalY=0 NormalZ=1 AngleXU=0 Radius=8
  constraints (2):
    c: Coincident(g0,g-1)
    c: Diameter(g0) = 16
FEATURE [PartDesign::Pad] Pad016
  Direction = (0,0,1)
  Length = 16
  Length2 = 10
  Profile = -> Sketch045
  ReferenceAxis = -> Sketch045 [N_Axis]
  Reversed = true
  Type = 0
  expr: Length = Spreadsheet.GearLengthBLDC - Spreadsheet.GearHeight
FEATURE [Sketcher::SketchObject] Sketch046
  FullyConstrained = true
  MapMode = 5
  Support = -> [XY_Plane039]
  expr: Constraints[4] = Spreadsheet.ShaftCouplerInnerDiameter
  expr: Constraints[5] = Spreadsheet.ShaftCouplerInnerDiameter / 2 - 1
  sketch-geometry (2):
    g0: ArcOfCircle CenterX=0 CenterY=0 CenterZ=0 NormalX=0 NormalY=0 NormalZ=1 AngleXU=0 Radius=4.075 StartAngle=2.28655 EndAngle=7.13823
    g1: LineSegment StartX=-2.67395 StartY=3.075 StartZ=0 EndX=2.67395 EndY=3.075 EndZ=0
  constraints (6):
    c: Coincident(g0,g-1)
    c: Horizontal(g1)
    c: Coincident(g0,g1)
    c: Coincident(g0,g1)
    c: Diameter(g0) = 8.15
    c: DistanceY(g0,g0) = 3.075
FEATURE [PartDesign::Pocket] Pocket027  label="ShaftPocket006"
  BaseFeature = -> Pad016
  Direction = (0,0,-1)
  Length = 11
  Length2 = 5
  Profile = -> Sketch046
  ReferenceAxis = -> Sketch046 [N_Axis]
  Type = 1
  expr: Length = Spreadsheet.GearShaftPocketDepth
FEATURE [PartDesign::Chamfer] Chamfer006  label="ShaftChamfer001"
  Angle = 45
  Base = -> Pocket027 [Edge6,Edge7]
  BaseFeature = -> Pocket027
  ChamferType = 0
  FlipDirection = false
  Size = 0.3
  Size2 = 1
  SupportTransform = false
  UseAllEdges = false
FEATURE [Sketcher::SketchObject] Sketch049
  AttachmentOffset = pos=(0,0,-9) rot=(0,0,1;0rad)
  FullyConstrained = true
  MapMode = 5
  Placement = pos=(0,9,2e-15) rot=(1,0,0;1.5708rad)
  Support = -> [XZ_Plane038]
  expr: .AttachmentOffset.Base.z = -Spreadsheet.GearTeethPocketDiameter / 2
  expr: Constraints[2] = Spreadsheet.GearLockBoltThreadDiameter
  expr: Constraints[4] = Spreadsheet.GearLockBoltSeparation
  expr: Constraints[5] = Spreadsheet.GearLockBoltPosition
  sketch-geometry (2):
    g0: Circle CenterX=0 CenterY=-4 CenterZ=0 NormalX=0 NormalY=0 NormalZ=1 AngleXU=0 Radius=2.1
    g1: Circle CenterX=0 CenterY=-12 CenterZ=0 NormalX=0 NormalY=0 NormalZ=1 AngleXU=0 Radius=2.1
  constraints (6):
    c: PointOnObject(g0,g-2)
    c: PointOnObject(g1,g-2)
    c: Diameter(g0) = 4.2
    c: Equal(g0,g1)
    c: DistanceY(g1,g0) = 8
    c: DistanceY(g0,g-1) = 4
FEATURE [PartDesign::Pocket] Pocket031  label="LockBoltPocket024"
  BaseFeature = -> Chamfer006
  Direction = (0,1,2e-16)
  Length = 9
  Length2 = 5
  Profile = -> Sketch049
  ReferenceAxis = -> Sketch049 [N_Axis]
  Reversed = true
  Type = 0
  expr: Length = Spreadsheet.GearTeethPocketDiameter / 2
FEATURE [PartDesign::FeaturePython] InvoluteGear002  # WARN: FeaturePython — macro-defined, semantics opaque (R4)
  AttacherType = Attacher::AttachEngine3D
  BaseFeature = -> Pocket031
  angular_backlash = 0
  backlash = 0
  beta = 0
  clearance = 0.25
  da = 20
  df = 15.5
  double_helix = false
  dw = 18
  head = 0
  head_fillet = 0
  height = 8
  module = 1
  numpoints = 6
  pressure_angle = 20
  properties_from_tool = false
  reversed_backlash = false
  root_fillet = 0
  shift = 0
  simple = false
  teeth = 18
  transverse_pitch = 3.14159
  undercut = false
  version = 0.0.4
  expr: angular_backlash = backlash / dw * 360° / pi
  expr: dw = teeth * module
  expr: height = Spreadsheet.GearHeight
  expr: module = Spreadsheet.GearModule
  expr: teeth = Spreadsheet.GearTeeth
FEATURE [PartDesign::ShapeBinder] ShapeBinder001  label="ShaftPocket007"
  Support = -> [Sketch046]
  TraceSupport = false
FEATURE [PartDesign::Pocket] Pocket032
  BaseFeature = -> InvoluteGear002
  Direction = (0,0,-1)
  Length = 5
  Length2 = 5
  Profile = -> ShapeBinder001
  Reversed = true
  Type = 1
FEATURE [PartDesign::Body] Body014
  Group = -> [Sketch045,Pad016,Sketch046,Pocket027,Chamfer006,Sketch049,Pocket031,InvoluteGear002,ShapeBinder001,Pocket032]
  Origin = -> Origin038
  Tip = -> Pocket032
COMPONENT P12 — recipe-attached ("CableLock", modeled in this document).
Construction recipe (the document's own serialized feature program — sketch geometry with constraints, then the solid features built on it; lengths are millimeters unless a unit is written):

FEATURE [Sketcher::SketchObject] Sketch050
  FullyConstrained = false
  MapMode = 5
  Support = -> [XY_Plane042]
  sketch-geometry (9):
    g0: ArcOfCircle CenterX=-3.86982 CenterY=0 CenterZ=0 NormalX=0 NormalY=0 NormalZ=1 AngleXU=0 Radius=2.75 StartAngle=3.79337 EndAngle=5.6314
    g1: ArcOfCircle CenterX=3.86982 CenterY=0 CenterZ=0 NormalX=0 NormalY=0 NormalZ=1 AngleXU=0 Radius=3.05 StartAngle=3.72029 EndAngle=5.70448
    g2: ArcOfCircle CenterX=0 CenterY=0 CenterZ=0 NormalX=0 NormalY=0 NormalZ=1 AngleXU=0 Radius=7 StartAngle=3.38222 EndAngle=6.04256
    g3: LineSegment StartX=-1.68356 StartY=-1.66816 StartZ=0 EndX=1.31644 EndY=-1.66816 EndZ=0
    g4: LineSegment StartX=-6.05608 StartY=-1.66816 StartZ=0 EndX=-6.79833 EndY=-1.66816 EndZ=0
    g5: LineSegment StartX=6.4232 StartY=-1.66816 StartZ=0 EndX=6.79833 EndY=-1.66816 EndZ=0
    g6: LineSegment StartX=-6.79833 StartY=-1.66816 StartZ=0 EndX=-6.79833 EndY=0 EndZ=0
    g7: LineSegment StartX=1.31644 StartY=-1.66816 StartZ=0 EndX=1.31644 EndY=0 EndZ=0
    g8: LineSegment StartX=6.79833 StartY=-1.66816 StartZ=0 EndX=6.79833 EndY=0 EndZ=0
  constraints (27):
    c: PointOnObject(g0,g-1)
    c: Diameter(g0) = 5.5
    c: Diameter(g1) = 6.1
    c: Symmetric(g0,g1,g-1)
    c: Coincident(g2,g-1)
    c: Diameter(g2) = 14
    c: Horizontal(g3)
    c: DistanceX(g3,g3) = 3
    c: Horizontal(g4)
    c: Coincident(g6,g4)
    c: PointOnObject(g6,g-1)
    c: Vertical(g6)
    c: Coincident(g7,g3)
    c: PointOnObject(g7,g-1)
    c: Coincident(g8,g5)
    c: PointOnObject(g8,g-1)
    c: Vertical(g8)
    c: Vertical(g7)
    c: Equal(g6,g7)
    c: Equal(g7,g8)
    c: Horizontal(g5)
    c: Coincident(g2,g5)
    c: Coincident(g2,g4)
    c: Coincident(g0,g3)
    c: Coincident(g0,g4)
    c: Coincident(g1,g3)
    c: Coincident(g1,g5)
FEATURE [PartDesign::Pad] Pad017
  Direction = (0,0,1)
  Length = 10
  Length2 = 10
  Profile = -> Sketch050
  ReferenceAxis = -> Sketch050 [N_Axis]
  Type = 0
FEATURE [Sketcher::SketchObject] Sketch051
  FullyConstrained = true
  MapMode = 5
  Placement = pos=(0,-1.66816,0) rot=(0,0.707107,0.707107;3.14159rad)
  sketch-geometry (1):
    g0: Circle CenterX=0 CenterY=5 CenterZ=0 NormalX=0 NormalY=0 NormalZ=1 AngleXU=0 Radius=1.25
  constraints (3):
    c: PointOnObject(g0,g-2)
    c: Diameter(g0) = 2.5
    c: DistanceY(g-1,g0) = 5
FEATURE [PartDesign::Pocket] Pocket033
  BaseFeature = -> Pad017
  Direction = (0,-1,2e-16)
  Length = 5
  Length2 = 5
  Profile = -> Sketch051
  ReferenceAxis = -> Sketch051 [N_Axis]
  Type = 1
FEATURE [PartDesign::Body] Body015
  Group = -> [Sketch050,Pad017,Sketch051,Pocket033]
  Origin = -> Origin041
  Tip = -> Pocket033
PROVENANCE & LICENSES
A FreeCAD (.FCStd) document from a public repository crawl; recipes are the document's own serialized feature recipes (and, for linked parts, companion documents' recipes).
License: gpl-3.0.
